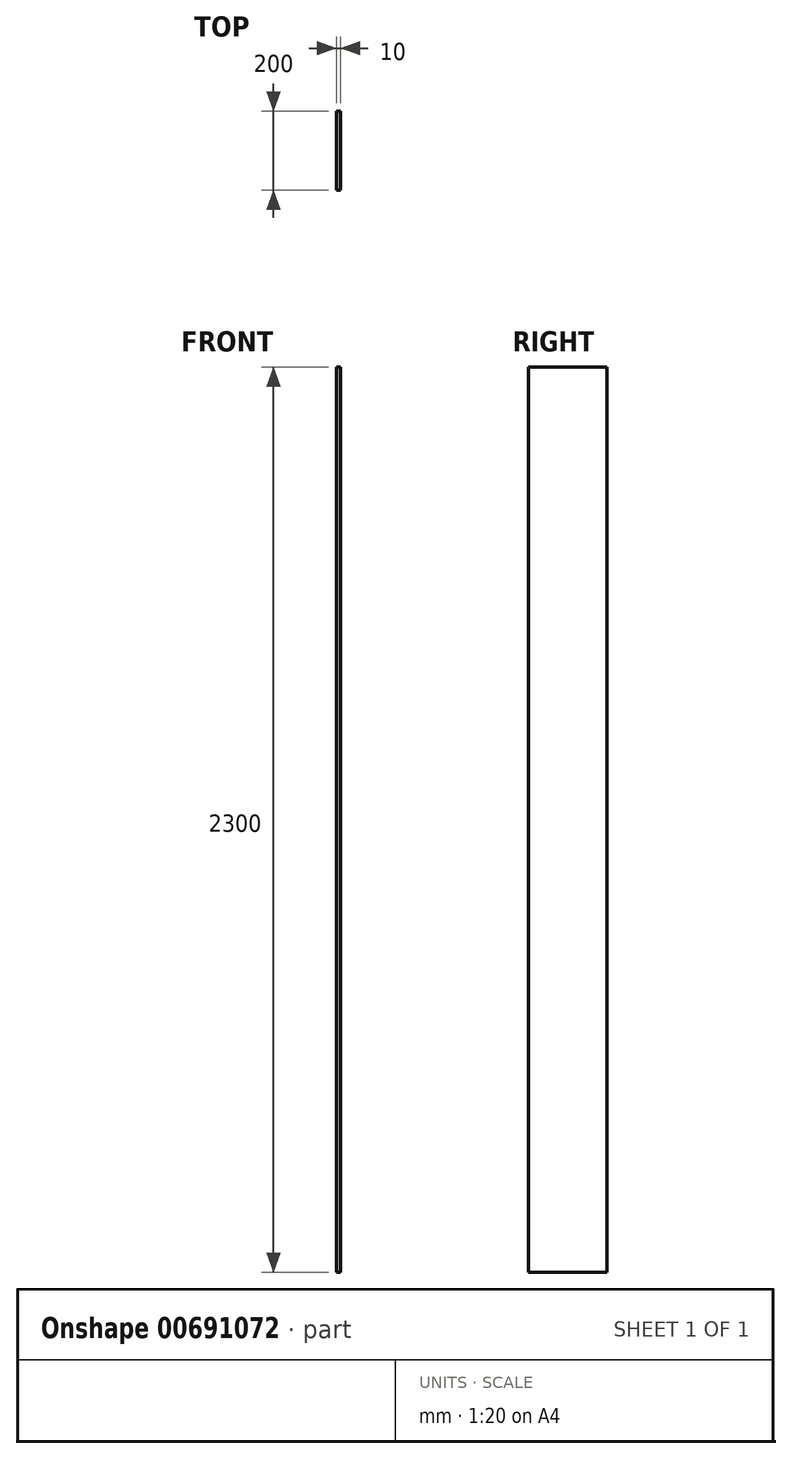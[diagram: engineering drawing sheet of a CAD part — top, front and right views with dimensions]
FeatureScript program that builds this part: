
annotation { "Feature Type Name" : "Feature", "Feature Type Description" : "" }
export const myFeature = defineFeature(function(context is Context, id is Id, definition is map)
    precondition{}
    {
        {
            var Q0;
            Q0=qCreatedBy(makeId("Right.planeOp"),FACE);
            var sketch = newSketch(context, id + "F0", { "sketchPlane" : qUnion([Q0])});
            skLineSegment(sketch, "E0.bottom", {"start": v(100, -1150) * mm, "end": v(-100, -1150) * mm});
            skLineSegment(sketch, "E0.top", {"start": v(100, 1150) * mm, "end": v(-100, 1150) * mm});
            skLineSegment(sketch, "E0.left", {"start": v(100, -1150) * mm, "end": v(100, 1150) * mm});
            skLineSegment(sketch, "E0.right", {"start": v(-100, -1150) * mm, "end": v(-100, 1150) * mm});
            skPoint(sketch, "E0.middle", {"position": v(0, 0) * mm});
            skSolve(sketch);
        }
        {
            var Q0;
            Q0=makeQuery(id+"F0.imprint","IMPRINT",FACE,{"disambiguationData":[TD([[makeQuery(id+"F0.imprint","IMPRINT",EDGE,{"derivedFrom":sQuery(id+"F0.wireOp",EDGE,"E0.bottom")}),-1.0]])]});
            extrude(context, id + "F1", {"entities" : qUnion([Q0]), "depth" : 10 * mm, "offsetDistance" : 25 * mm});
        }
    });
